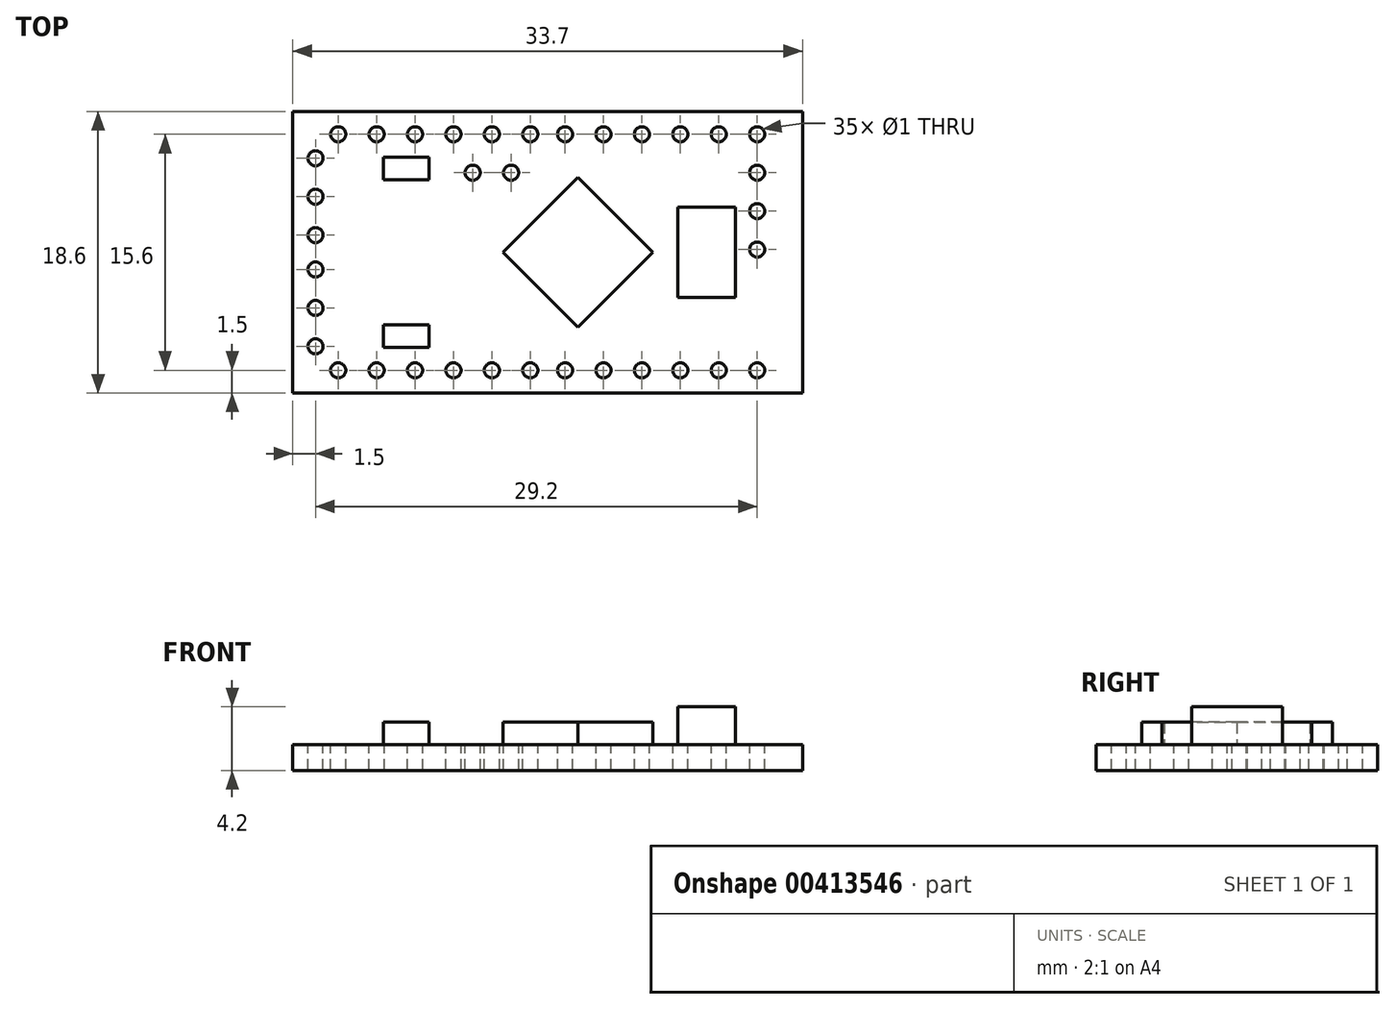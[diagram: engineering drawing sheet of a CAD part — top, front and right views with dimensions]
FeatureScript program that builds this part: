
annotation { "Feature Type Name" : "Feature", "Feature Type Description" : "" }
export const myFeature = defineFeature(function(context is Context, id is Id, definition is map)
    precondition{}
    {
        {
            var Q0;
            Q0=qCreatedBy(makeId("Top.planeOp"),FACE);
            var sketch = newSketch(context, id + "F0", { "sketchPlane" : qUnion([Q0])});
            skLineSegment(sketch, "E0.bottom", {"start": v(16.85, 9.3) * mm, "end": v(-16.85, 9.3) * mm});
            skLineSegment(sketch, "E0.top", {"start": v(16.85, -9.3) * mm, "end": v(-16.85, -9.3) * mm});
            skLineSegment(sketch, "E0.left", {"start": v(16.85, 9.3) * mm, "end": v(16.85, -9.3) * mm});
            skLineSegment(sketch, "E0.right", {"start": v(-16.85, 9.3) * mm, "end": v(-16.85, -9.3) * mm});
            skPoint(sketch, "E0.middle", {"position": v(0, 0) * mm});
            skSolve(sketch);
        }
        {
            var Q0;
            Q0 = qSketchRegion(id + "F0", true);
            extrude(context, id + "F1", {"entities" : qUnion([Q0]), "depth" : 1.7 * mm});
        }
        {
            var Q0;
            Q0=makeQuery(id+"F1.opExtrude","CAP_FACE",FACE,{"disambiguationData":[OSD([sQuery(id+"F0.wireOp",EDGE,"E0.bottom"),sQuery(id+"F0.wireOp",EDGE,"E0.top"),sQuery(id+"F0.wireOp",EDGE,"E0.left"),sQuery(id+"F0.wireOp",EDGE,"E0.right")])],"isStart":false});
            var sketch = newSketch(context, id + "F2", { "sketchPlane" : qUnion([Q0])});
            skCircle(sketch, "E1", {"center": v(-13.85, 7.8) * mm, "radius": 0.5 * mm});
            skCircle(sketch, "E2", {"center": v(-11.3, 7.8) * mm, "radius": 0.5 * mm});
            skCircle(sketch, "E3", {"center": v(-8.77, 7.8) * mm, "radius": 0.5 * mm});
            skCircle(sketch, "E4", {"center": v(-6.23, 7.8) * mm, "radius": 0.5 * mm});
            skCircle(sketch, "E5", {"center": v(-3.69, 7.8) * mm, "radius": 0.5 * mm});
            skCircle(sketch, "E6", {"center": v(-1.15, 7.8) * mm, "radius": 0.5 * mm});
            skCircle(sketch, "E7.MirrorC", {"center": v(1.15, 7.8) * mm, "radius": 0.5 * mm});
            skCircle(sketch, "E8.MirrorC", {"center": v(3.69, 7.8) * mm, "radius": 0.5 * mm});
            skCircle(sketch, "E9.MirrorC", {"center": v(6.23, 7.8) * mm, "radius": 0.5 * mm});
            skCircle(sketch, "E10.MirrorC", {"center": v(8.77, 7.8) * mm, "radius": 0.5 * mm});
            skCircle(sketch, "E11.MirrorC", {"center": v(11.3, 7.8) * mm, "radius": 0.5 * mm});
            skCircle(sketch, "E12.MirrorC", {"center": v(13.85, 7.8) * mm, "radius": 0.5 * mm});
            skCircle(sketch, "E13.MirrorC", {"center": v(13.85, -7.8) * mm, "radius": 0.5 * mm});
            skCircle(sketch, "E14.MirrorC", {"center": v(11.3, -7.8) * mm, "radius": 0.5 * mm});
            skCircle(sketch, "E15.MirrorC", {"center": v(8.77, -7.8) * mm, "radius": 0.5 * mm});
            skCircle(sketch, "E16.MirrorC", {"center": v(6.23, -7.8) * mm, "radius": 0.5 * mm});
            skCircle(sketch, "E17.MirrorC", {"center": v(3.69, -7.8) * mm, "radius": 0.5 * mm});
            skCircle(sketch, "E18.MirrorC", {"center": v(1.15, -7.8) * mm, "radius": 0.5 * mm});
            skCircle(sketch, "E19.MirrorC", {"center": v(-1.15, -7.8) * mm, "radius": 0.5 * mm});
            skCircle(sketch, "E20.MirrorC", {"center": v(-3.69, -7.8) * mm, "radius": 0.5 * mm});
            skCircle(sketch, "E21.MirrorC", {"center": v(-6.23, -7.8) * mm, "radius": 0.5 * mm});
            skCircle(sketch, "E22.MirrorC", {"center": v(-8.77, -7.8) * mm, "radius": 0.5 * mm});
            skCircle(sketch, "E23.MirrorC", {"center": v(-11.3, -7.8) * mm, "radius": 0.5 * mm});
            skCircle(sketch, "E24.MirrorC", {"center": v(-13.85, -7.8) * mm, "radius": 0.5 * mm});
            skCircle(sketch, "E25", {"center": v(13.85, 5.26) * mm, "radius": 0.5 * mm});
            skCircle(sketch, "E26", {"center": v(13.85, 2.72) * mm, "radius": 0.5 * mm});
            skCircle(sketch, "E27", {"center": v(13.85, 0.18) * mm, "radius": 0.5 * mm});
            skCircle(sketch, "E28", {"center": v(-15.35, 6.22) * mm, "radius": 0.5 * mm});
            skCircle(sketch, "E29", {"center": v(-15.35, 3.68) * mm, "radius": 0.5 * mm});
            skCircle(sketch, "E30", {"center": v(-15.35, 1.14) * mm, "radius": 0.5 * mm});
            skCircle(sketch, "E31.MirrorC", {"center": v(-15.35, -1.14) * mm, "radius": 0.5 * mm});
            skCircle(sketch, "E32.MirrorC", {"center": v(-15.35, -3.68) * mm, "radius": 0.5 * mm});
            skCircle(sketch, "E33.MirrorC", {"center": v(-15.35, -6.22) * mm, "radius": 0.5 * mm});
            skPoint(sketch, "E34", {"position": v(2.54, 0) * mm});
            skCircle(sketch, "E35", {"center": v(-4.96, 5.26) * mm, "radius": 0.5 * mm});
            skCircle(sketch, "E36", {"center": v(-2.42, 5.26) * mm, "radius": 0.5 * mm});
            skSolve(sketch);
        }
        {
            var Q0;
            Q0 = qSketchRegion(id + "F2", true);
            extrude(context, id + "F3", {"entities" : qUnion([Q0]), "operationType" : NewBodyOperationType.REMOVE, "endBound" : BoundingType.THROUGH_ALL, "oppositeDirection" : true, "depth" : 25 * mm});
        }
        {
            var Q0;
            Q0=makeQuery(id+"F1.opExtrude","CAP_FACE",FACE,{"disambiguationData":[OSD([sQuery(id+"F0.wireOp",EDGE,"E0.bottom"),sQuery(id+"F0.wireOp",EDGE,"E0.top"),sQuery(id+"F0.wireOp",EDGE,"E0.left"),sQuery(id+"F0.wireOp",EDGE,"E0.right")])],"isStart":false});
            var sketch = newSketch(context, id + "F4", { "sketchPlane" : qUnion([Q0])});
            skPoint(sketch, "E37", {"position": v(2, 0) * mm});
            skCircle(sketch, "E38.cCircle", {"center": v(2, 0) * mm, "radius": 3.5 * mm, "construction": true});
            skLineSegment(sketch, "E38.0", {"start": v(2, 4.95) * mm, "end": v(6.95, 0) * mm});
            skLineSegment(sketch, "E38.1", {"start": v(6.95, 0) * mm, "end": v(2, -4.95) * mm});
            skLineSegment(sketch, "E38.2", {"start": v(2, -4.95) * mm, "end": v(-2.95, 0) * mm});
            skLineSegment(sketch, "E38.3", {"start": v(-2.95, 0) * mm, "end": v(2, 4.95) * mm});
            skPoint(sketch, "E38.0.midPoint", {"position": v(4.47, 2.47) * mm});
            skLineSegment(sketch, "E39.bottom", {"start": v(12.4, 3) * mm, "end": v(8.6, 3) * mm});
            skLineSegment(sketch, "E39.top", {"start": v(12.4, -3) * mm, "end": v(8.6, -3) * mm});
            skLineSegment(sketch, "E39.left", {"start": v(12.4, 3) * mm, "end": v(12.4, -3) * mm});
            skLineSegment(sketch, "E39.right", {"start": v(8.6, 3) * mm, "end": v(8.6, -3) * mm});
            skPoint(sketch, "E39.middle", {"position": v(10.5, 0) * mm});
            skLineSegment(sketch, "E40.bottom", {"start": v(-10.85, 6.3) * mm, "end": v(-7.85, 6.3) * mm});
            skLineSegment(sketch, "E40.top", {"start": v(-10.85, 4.8) * mm, "end": v(-7.85, 4.8) * mm});
            skLineSegment(sketch, "E40.left", {"start": v(-10.85, 6.3) * mm, "end": v(-10.85, 4.8) * mm});
            skLineSegment(sketch, "E40.right", {"start": v(-7.85, 6.3) * mm, "end": v(-7.85, 4.8) * mm});
            skLineSegment(sketch, "E41.MirrorCS", {"start": v(-7.85, -6.3) * mm, "end": v(-7.85, -4.8) * mm});
            skLineSegment(sketch, "E42.MirrorCS", {"start": v(-10.85, -4.8) * mm, "end": v(-7.85, -4.8) * mm});
            skLineSegment(sketch, "E43.MirrorCS", {"start": v(-10.85, -6.3) * mm, "end": v(-7.85, -6.3) * mm});
            skLineSegment(sketch, "E44.MirrorCS", {"start": v(-10.85, -6.3) * mm, "end": v(-10.85, -4.8) * mm});
            skSolve(sketch);
        }
        {
            var Q0;
            Q0=makeQuery(id+"F4.imprint","IMPRINT",FACE,{"disambiguationData":[TD([[makeQuery(id+"F4.imprint","IMPRINT",EDGE,{"derivedFrom":sQuery(id+"F4.wireOp",EDGE,"E38.0")}),-1.0]])]});
            extrude(context, id + "F5", {"entities" : qUnion([Q0]), "operationType" : NewBodyOperationType.ADD, "depth" : 1.5 * mm});
        }
        {
            var Q0;
            Q0=makeQuery(id+"F4.imprint","IMPRINT",FACE,{"disambiguationData":[TD([[makeQuery(id+"F4.imprint","IMPRINT",EDGE,{"derivedFrom":sQuery(id+"F4.wireOp",EDGE,"E39.bottom")}),1.0]])]});
            extrude(context, id + "F6", {"entities" : qUnion([Q0]), "operationType" : NewBodyOperationType.ADD, "depth" : 2.5 * mm});
        }
        {
            var Q0;
            Q0=makeQuery(id+"F4.imprint","IMPRINT",FACE,{"disambiguationData":[TD([[makeQuery(id+"F4.imprint","IMPRINT",EDGE,{"derivedFrom":sQuery(id+"F4.wireOp",EDGE,"E40.bottom")}),-1.0]])]});
            var Q1;
            Q1=makeQuery(id+"F4.imprint","IMPRINT",FACE,{"disambiguationData":[TD([[makeQuery(id+"F4.imprint","IMPRINT",EDGE,{"derivedFrom":sQuery(id+"F4.wireOp",EDGE,"E41.MirrorCS")}),1.0]])]});
            extrude(context, id + "F7", {"entities" : qUnion([Q0, Q1]), "operationType" : NewBodyOperationType.ADD, "depth" : 1.5 * mm});
        }
    });
